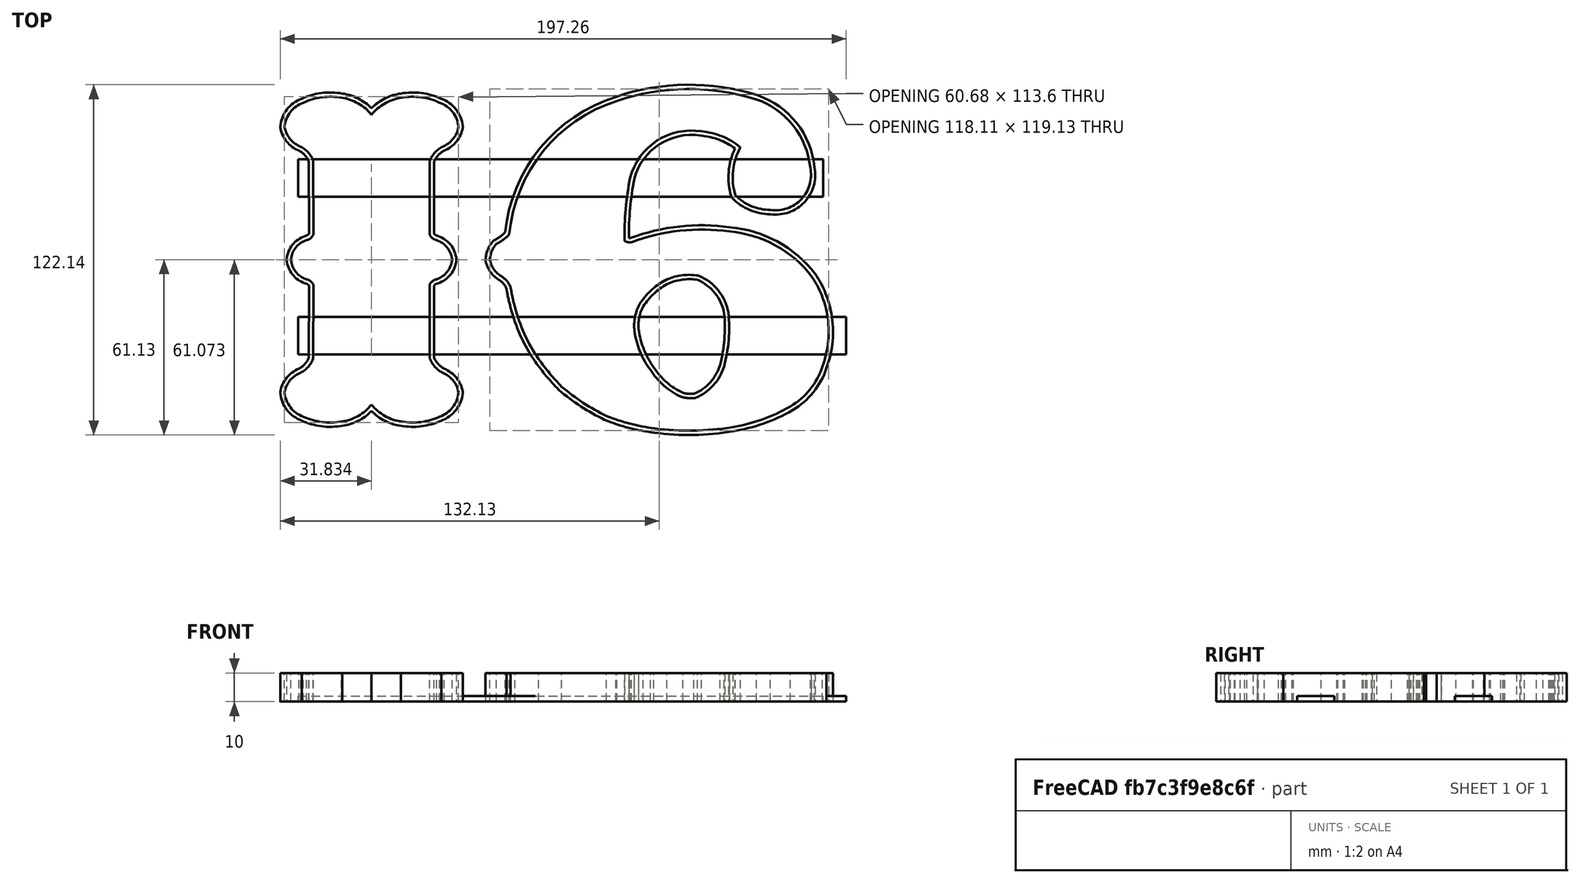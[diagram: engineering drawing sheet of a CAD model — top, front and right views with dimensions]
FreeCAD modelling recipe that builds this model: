
FCSTD DOCUMENT  (FreeCAD 0.20R27319 (Git))
Label: NumberCutter_16
License: All rights reserved
LicenseURL: http://en.wikipedia.org/wiki/All_rights_reserved
objects: Part::Box×2, Image::ImagePlane×1, Sketcher::SketchObject×1, PartDesign::Body×1, Part::Offset2D×1, Part::Extrusion×1
note: 6 computed .brp shape members not serialized (recipe doc carries the construction recipe); baked Part::Feature solids carry a one-line shape summary decoded from their .brp

FEATURE [Image::ImagePlane] ImagePlane
  XSize = 191
  YSize = 120
FEATURE [Sketcher::SketchObject] Sketch001
  FullyConstrained = false
  MapMode = 5
  Support = -> [XY_Plane]
  sketch-geometry (67):
    g0: LineSegment StartX=-44.0949 StartY=34.442 StartZ=0 EndX=-44.1561 EndY=8.72012 EndZ=0
    g1: ArcOfCircle CenterX=-44.2555 CenterY=-0.704352 CenterZ=0 NormalX=0 NormalY=0 NormalZ=1 AngleXU=0 Radius=7.94489 StartAngle=0.0887712 EndAngle=1.24847
    g2: ArcOfCircle CenterX=-41.0719 CenterY=10.1762 CenterZ=0 NormalX=0 NormalY=0 NormalZ=1 AngleXU=0 Radius=3.4106 StartAngle=3.58267 EndAngle=4.51561
    g3: ArcOfCircle CenterX=-51.9319 CenterY=40.6835 CenterZ=0 NormalX=0 NormalY=0 NormalZ=1 AngleXU=0 Radius=15.899 StartAngle=1.69919 EndAngle=2.47486
    g4: ArcOfCircle CenterX=-50.005 CenterY=34.6117 CenterZ=0 NormalX=0 NormalY=0 NormalZ=1 AngleXU=0 Radius=22.1964 StartAngle=1.13736 EndAngle=1.75028
    g5: ArcOfCircle CenterX=-43.9763 CenterY=45.3788 CenterZ=0 NormalX=0 NormalY=0 NormalZ=1 AngleXU=0 Radius=9.93843 StartAngle=0.0999134 EndAngle=1.23302
    g6: ArcOfCircle CenterX=-43.0231 CenterY=47.8373 CenterZ=0 NormalX=0 NormalY=0 NormalZ=1 AngleXU=0 Radius=9.05532 StartAngle=5.08333 EndAngle=6.12044
    g7: ArcOfCircle CenterX=-35.5185 CenterY=31.2976 CenterZ=0 NormalX=0 NormalY=0 NormalZ=1 AngleXU=0 Radius=9.13456 StartAngle=2.05128 EndAngle=2.79018
    g8: LineSegment StartX=-84.7572 StartY=34.442 StartZ=0 EndX=-84.6959 EndY=8.72012 EndZ=0
    g9: ArcOfCircle CenterX=-84.5965 CenterY=-0.704352 CenterZ=0 NormalX=0 NormalY=0 NormalZ=1 AngleXU=0 Radius=7.94489 StartAngle=1.89313 EndAngle=3.05282
    g10: ArcOfCircle CenterX=-87.7801 CenterY=10.1762 CenterZ=0 NormalX=0 NormalY=0 NormalZ=1 AngleXU=0 Radius=3.4106 StartAngle=4.90916 EndAngle=5.8421
    g11: ArcOfCircle CenterX=-76.9201 CenterY=40.6835 CenterZ=0 NormalX=0 NormalY=0 NormalZ=1 AngleXU=0 Radius=15.899 StartAngle=0.666734 EndAngle=1.4424
    g12: ArcOfCircle CenterX=-78.847 CenterY=34.6117 CenterZ=0 NormalX=0 NormalY=0 NormalZ=1 AngleXU=0 Radius=22.1964 StartAngle=1.39131 EndAngle=2.00423
    g13: ArcOfCircle CenterX=-84.8757 CenterY=45.3788 CenterZ=0 NormalX=0 NormalY=0 NormalZ=1 AngleXU=0 Radius=9.93843 StartAngle=1.90858 EndAngle=3.04168
    g14: ArcOfCircle CenterX=-85.8289 CenterY=47.8373 CenterZ=0 NormalX=0 NormalY=0 NormalZ=1 AngleXU=0 Radius=9.05532 StartAngle=3.30434 EndAngle=4.34144
    g15: ArcOfCircle CenterX=-93.3335 CenterY=31.2976 CenterZ=0 NormalX=0 NormalY=0 NormalZ=1 AngleXU=0 Radius=9.13456 StartAngle=0.35141 EndAngle=1.09032
    g16: LineSegment StartX=-44.0949 StartY=-34.442 StartZ=0 EndX=-44.1561 EndY=-8.72012 EndZ=0
    g17: ArcOfCircle CenterX=-44.2555 CenterY=0.704352 CenterZ=0 NormalX=0 NormalY=0 NormalZ=1 AngleXU=0 Radius=7.94489 StartAngle=5.03472 EndAngle=6.19441
    g18: ArcOfCircle CenterX=-41.0719 CenterY=-10.1762 CenterZ=0 NormalX=0 NormalY=0 NormalZ=1 AngleXU=0 Radius=3.4106 StartAngle=1.76757 EndAngle=2.70051
    g19: ArcOfCircle CenterX=-51.9319 CenterY=-40.6835 CenterZ=0 NormalX=0 NormalY=0 NormalZ=1 AngleXU=0 Radius=15.899 StartAngle=3.80833 EndAngle=4.58399
    g20: ArcOfCircle CenterX=-50.005 CenterY=-34.6117 CenterZ=0 NormalX=0 NormalY=0 NormalZ=1 AngleXU=0 Radius=22.1964 StartAngle=4.5329 EndAngle=5.14582
    g21: ArcOfCircle CenterX=-43.9763 CenterY=-45.3788 CenterZ=0 NormalX=0 NormalY=0 NormalZ=1 AngleXU=0 Radius=9.93843 StartAngle=5.05017 EndAngle=6.18327
    g22: ArcOfCircle CenterX=-43.0231 CenterY=-47.8373 CenterZ=0 NormalX=0 NormalY=0 NormalZ=1 AngleXU=0 Radius=9.05532 StartAngle=0.162744 EndAngle=1.19985
    g23: ArcOfCircle CenterX=-35.5185 CenterY=-31.2976 CenterZ=0 NormalX=0 NormalY=0 NormalZ=1 AngleXU=0 Radius=9.13456 StartAngle=3.493 EndAngle=4.23191
    g24: LineSegment StartX=-84.7572 StartY=-34.442 StartZ=0 EndX=-84.6959 EndY=-8.72012 EndZ=0
    g25: ArcOfCircle CenterX=-84.5965 CenterY=0.704352 CenterZ=0 NormalX=0 NormalY=0 NormalZ=1 AngleXU=0 Radius=7.94489 StartAngle=3.23036 EndAngle=4.39006
    g26: ArcOfCircle CenterX=-87.7801 CenterY=-10.1762 CenterZ=0 NormalX=0 NormalY=0 NormalZ=1 AngleXU=0 Radius=3.4106 StartAngle=0.441081 EndAngle=1.37402
    g27: ArcOfCircle CenterX=-76.9201 CenterY=-40.6835 CenterZ=0 NormalX=0 NormalY=0 NormalZ=1 AngleXU=0 Radius=15.899 StartAngle=4.84079 EndAngle=5.61645
    g28: ArcOfCircle CenterX=-78.847 CenterY=-34.6117 CenterZ=0 NormalX=0 NormalY=0 NormalZ=1 AngleXU=0 Radius=22.1964 StartAngle=4.27895 EndAngle=4.89188
    g29: ArcOfCircle CenterX=-84.8757 CenterY=-45.3788 CenterZ=0 NormalX=0 NormalY=0 NormalZ=1 AngleXU=0 Radius=9.93843 StartAngle=3.24151 EndAngle=4.37461
    g30: ArcOfCircle CenterX=-85.8289 CenterY=-47.8373 CenterZ=0 NormalX=0 NormalY=0 NormalZ=1 AngleXU=0 Radius=9.05532 StartAngle=1.94174 EndAngle=2.97885
    g31: ArcOfCircle CenterX=-93.3335 CenterY=-31.2976 CenterZ=0 NormalX=0 NormalY=0 NormalZ=1 AngleXU=0 Radius=9.13456 StartAngle=5.19287 EndAngle=5.93178
    g32: ArcOfCircle CenterX=-14.3118 CenterY=-0.477089 CenterZ=0 NormalX=0 NormalY=0 NormalZ=1 AngleXU=0 Radius=8.88675 StartAngle=2.40162 EndAngle=3.08788
    g33: ArcOfCircle CenterX=-26.693 CenterY=17.7972 CenterZ=0 NormalX=0 NormalY=0 NormalZ=1 AngleXU=0 Radius=13.5907 StartAngle=5.1548 EndAngle=5.56991
    g34: ArcOfCircle CenterX=37.4429 CenterY=3.76243 CenterZ=0 NormalX=0 NormalY=0 NormalZ=1 AngleXU=0 Radius=54.1032 StartAngle=1.87661 EndAngle=3.0464
    g35: ArcOfCircle CenterX=46.2531 CenterY=-18.3508 CenterZ=0 NormalX=0 NormalY=0 NormalZ=1 AngleXU=0 Radius=77.8624 StartAngle=1.26469 EndAngle=1.89901
    g36: ArcOfCircle CenterX=60.5001 CenterY=29.3101 CenterZ=0 NormalX=0 NormalY=0 NormalZ=1 AngleXU=0 Radius=28.1345 StartAngle=0.0982451 EndAngle=1.23706
    g37: ArcOfCircle CenterX=76.4612 CenterY=29.5329 CenterZ=0 NormalX=0 NormalY=0 NormalZ=1 AngleXU=0 Radius=12.3022 StartAngle=4.56544 EndAngle=6.49089
    g38: ArcOfCircle CenterX=74.616 CenterY=34.4646 CenterZ=0 NormalX=0 NormalY=0 NormalZ=1 AngleXU=0 Radius=17.1014 StartAngle=3.91734 EndAngle=4.71496
    g39: ArcOfCircle CenterX=82.9352 CenterY=28.7211 CenterZ=0 NormalX=0 NormalY=0 NormalZ=1 AngleXU=0 Radius=21.4529 StartAngle=2.63178 EndAngle=3.43632
    g40: ArcOfCircle CenterX=48.4504 CenterY=19.9812 CenterZ=0 NormalX=0 NormalY=0 NormalZ=1 AngleXU=0 Radius=24.8469 StartAngle=0.883715 EndAngle=1.48558
    g41: ArcOfCircle CenterX=47.0715 CenterY=22.9255 CenterZ=0 NormalX=0 NormalY=0 NormalZ=1 AngleXU=0 Radius=22.0904 StartAngle=1.41197 EndAngle=2.88283
    g42: ArcOfCircle CenterX=133.219 CenterY=7.96319 CenterZ=0 NormalX=0 NormalY=0 NormalZ=1 AngleXU=0 Radius=109.461 StartAngle=2.95213 EndAngle=3.1543
    g43: ArcOfCircle CenterX=25.6086 CenterY=9.36331 CenterZ=0 NormalX=0 NormalY=0 NormalZ=1 AngleXU=0 Radius=3.34395 StartAngle=4.12901 EndAngle=4.88585
    g44: ArcOfCircle CenterX=50.6675 CenterY=-59.4009 CenterZ=0 NormalX=0 NormalY=0 NormalZ=1 AngleXU=0 Radius=69.8981 StartAngle=1.43149 EndAngle=1.92863
    g45: ArcOfCircle CenterX=56.849 CenterY=-30.6384 CenterZ=0 NormalX=0 NormalY=0 NormalZ=1 AngleXU=0 Radius=40.6116 StartAngle=0.652321 EndAngle=1.48392
    g46: ArcOfCircle CenterX=59.698 CenterY=-25.5465 CenterZ=0 NormalX=0 NormalY=0 NormalZ=1 AngleXU=0 Radius=35.3327 StartAngle=0.183618 EndAngle=0.586697
    g47: ArcOfCircle CenterX=59.1415 CenterY=-25.0675 CenterZ=0 NormalX=0 NormalY=0 NormalZ=1 AngleXU=0 Radius=35.797 StartAngle=5.93472 EndAngle=6.45081
    g48: ArcOfCircle CenterX=68.5744 CenterY=-29.2445 CenterZ=0 NormalX=0 NormalY=0 NormalZ=1 AngleXU=0 Radius=25.5145 StartAngle=5.24515 EndAngle=5.96235
    g49: ArcOfCircle CenterX=51.6917 CenterY=0.785216 CenterZ=0 NormalX=0 NormalY=0 NormalZ=1 AngleXU=0 Radius=59.9615 StartAngle=4.87202 EndAngle=5.23332
    g50: ArcOfCircle CenterX=46.2762 CenterY=32.5071 CenterZ=0 NormalX=0 NormalY=0 NormalZ=1 AngleXU=0 Radius=92.1414 StartAngle=4.58208 EndAngle=4.87532
    g51: ArcOfCircle CenterX=42.2772 CenterY=6.73465 CenterZ=0 NormalX=0 NormalY=0 NormalZ=1 AngleXU=0 Radius=66.0707 StartAngle=4.32807 EndAngle=4.5914
    g52: ArcOfCircle CenterX=49.2357 CenterY=11.0915 CenterZ=0 NormalX=0 NormalY=0 NormalZ=1 AngleXU=0 Radius=72.8781 StartAngle=4.00513 EndAngle=4.26192
    g53: ArcOfCircle CenterX=58.6775 CenterY=11.2759 CenterZ=0 NormalX=0 NormalY=0 NormalZ=1 AngleXU=0 Radius=79.4671 StartAngle=3.75871 EndAngle=3.9162
    g54: ArcOfCircle CenterX=40.8052 CenterY=-2.28447 CenterZ=0 NormalX=0 NormalY=0 NormalZ=1 AngleXU=0 Radius=57.0486 StartAngle=3.39119 EndAngle=3.74615
    g55: ArcOfCircle CenterX=38.9149 CenterY=-1.25283 CenterZ=0 NormalX=0 NormalY=0 NormalZ=1 AngleXU=0 Radius=55.4911 StartAngle=3.29753 EndAngle=3.41762
    g56: ArcOfCircle CenterX=-22.8727 CenterY=-12.1054 CenterZ=0 NormalX=0 NormalY=0 NormalZ=1 AngleXU=0 Radius=7.31918 StartAngle=0.310212 EndAngle=1.03585
    g57: ArcOfCircle CenterX=-14.7928 CenterY=1.53128 CenterZ=0 NormalX=0 NormalY=0 NormalZ=1 AngleXU=0 Radius=8.5315 StartAngle=3.32206 EndAngle=4.17754
    g58: ArcOfCircle CenterX=43.1477 CenterY=-21.4122 CenterZ=0 NormalX=0 NormalY=0 NormalZ=1 AngleXU=0 Radius=15.5785 StartAngle=0.172564 EndAngle=1.17541
    g59: ArcOfCircle CenterX=7.15552 CenterY=-23.7166 CenterZ=0 NormalX=0 NormalY=0 NormalZ=1 AngleXU=0 Radius=51.5801 StartAngle=6.02427 EndAngle=6.37987
    g60: ArcOfCircle CenterX=41.7256 CenterY=-31.9954 CenterZ=0 NormalX=0 NormalY=0 NormalZ=1 AngleXU=0 Radius=16.0651 StartAngle=5.1123 EndAngle=5.97144
    g61: ArcOfCircle CenterX=47.0754 CenterY=-35.0507 CenterZ=0 NormalX=0 NormalY=0 NormalZ=1 AngleXU=0 Radius=11.777 StartAngle=4.45535 EndAngle=4.78931
    g62: ArcOfCircle CenterX=54.4423 CenterY=-24.4593 CenterZ=0 NormalX=0 NormalY=0 NormalZ=1 AngleXU=0 Radius=24.3009 StartAngle=3.71228 EndAngle=4.27192
    g63: ArcOfCircle CenterX=57.1795 CenterY=-20.5968 CenterZ=0 NormalX=0 NormalY=0 NormalZ=1 AngleXU=0 Radius=28.7456 StartAngle=3.27924 EndAngle=3.77395
    g64: ArcOfCircle CenterX=42.8143 CenterY=-22.967 CenterZ=0 NormalX=0 NormalY=0 NormalZ=1 AngleXU=0 Radius=14.196 StartAngle=2.64973 EndAngle=3.2527
    g65: ArcOfCircle CenterX=50.3544 CenterY=-29.4284 CenterZ=0 NormalX=0 NormalY=0 NormalZ=1 AngleXU=0 Radius=23.9889 StartAngle=2.08701 EndAngle=2.56064
    g66: ArcOfCircle CenterX=46.2508 CenterY=-24.6241 CenterZ=0 NormalX=0 NormalY=0 NormalZ=1 AngleXU=0 Radius=17.8255 StartAngle=1.40755 EndAngle=2.01978
  constraints (69):
    c: PointOnObject(g1,g-1)
    c: Coincident(g2,g1)
    c: Coincident(g4,g3)
    c: Coincident(g5,g4)
    c: Coincident(g6,g5)
    c: Coincident(g7,g6)
    c: Coincident(g7,g0)
    c: Coincident(g10,g9)
    c: Coincident(g12,g11)
    c: Coincident(g13,g12)
    c: Coincident(g14,g13)
    c: Coincident(g15,g14)
    c: Coincident(g15,g8)
    c: Coincident(g18,g17)
    c: Coincident(g20,g19)
    c: Coincident(g21,g20)
    c: Coincident(g22,g21)
    c: Coincident(g23,g22)
    c: Coincident(g23,g16)
    c: Coincident(g26,g25)
    c: Coincident(g28,g27)
    c: Coincident(g29,g28)
    c: Coincident(g30,g29)
    c: Coincident(g31,g30)
    c: Coincident(g31,g24)
    c: PointOnObject(g32,g-1)
    c: Coincident(g33,g32)
    c: Coincident(g34,g33)
    c: Coincident(g35,g34)
    c: Coincident(g36,g35)
    c: Coincident(g37,g36)
    c: Coincident(g38,g37)
    c: Coincident(g40,g39)
    c: Coincident(g41,g40)
    c: Coincident(g42,g41)
    c: Coincident(g44,g43)
    c: Coincident(g45,g44)
    c: Coincident(g46,g45)
    c: Coincident(g47,g46)
    c: Coincident(g48,g47)
    c: Coincident(g49,g48)
    c: Coincident(g50,g49)
    c: Coincident(g51,g50)
    c: Coincident(g52,g51)
    c: Coincident(g53,g52)
    c: Coincident(g54,g53)
    c: Coincident(g55,g54)
    c: Coincident(g56,g55)
    c: Coincident(g57,g32)
    c: Coincident(g57,g56)
    c: Coincident(g59,g58)
    c: Coincident(g60,g59)
    c: Coincident(g61,g60)
    c: Coincident(g62,g61)
    c: Coincident(g63,g62)
    c: Coincident(g64,g63)
    c: Coincident(g65,g64)
    c: Coincident(g66,g65)
    c: Coincident(g66,g58)
    c: Coincident(g42,g43)
    c: Coincident(g3,g11)
    c: Coincident(g8,g10)
    c: Coincident(g9,g25)
    c: Coincident(g24,g26)
    c: Coincident(g19,g27)
    c: Coincident(g1,g17)
    c: Coincident(g16,g18)
    c: Coincident(g0,g2)
    c: Coincident(g38,g39)
FEATURE [PartDesign::Body] Body
  Group = -> [Sketch001]
  Origin = -> Origin
FEATURE [Part::Offset2D] Offset2D
  Fill = true
  Intersection = false
  Join = 0
  Mode = 1
  SelfIntersection = false
  Source = -> Sketch001
  Value = 1.5
FEATURE [Part::Extrusion] Extrude
  Base = -> Offset2D
  Dir = (0,0,1)
  DirMode = 2
  FaceMakerClass = Part::FaceMakerBullseye
  LengthFwd = 10
  LengthRev = 0
  Solid = false
  Symmetric = false
FEATURE [Part::Box] Box  label="Cube"
  AttacherType = Attacher::AttachEngine3D
  Height = 2
  Length = 183
  Placement = pos=(-90,22,0) rot=(0,0,1;0rad)
  Width = 13
FEATURE [Part::Box] Box001  label="Cube001"
  AttacherType = Attacher::AttachEngine3D
  Height = 2
  Length = 191
  Placement = pos=(-90,-33,0) rot=(0,0,1;0rad)
  Width = 13
